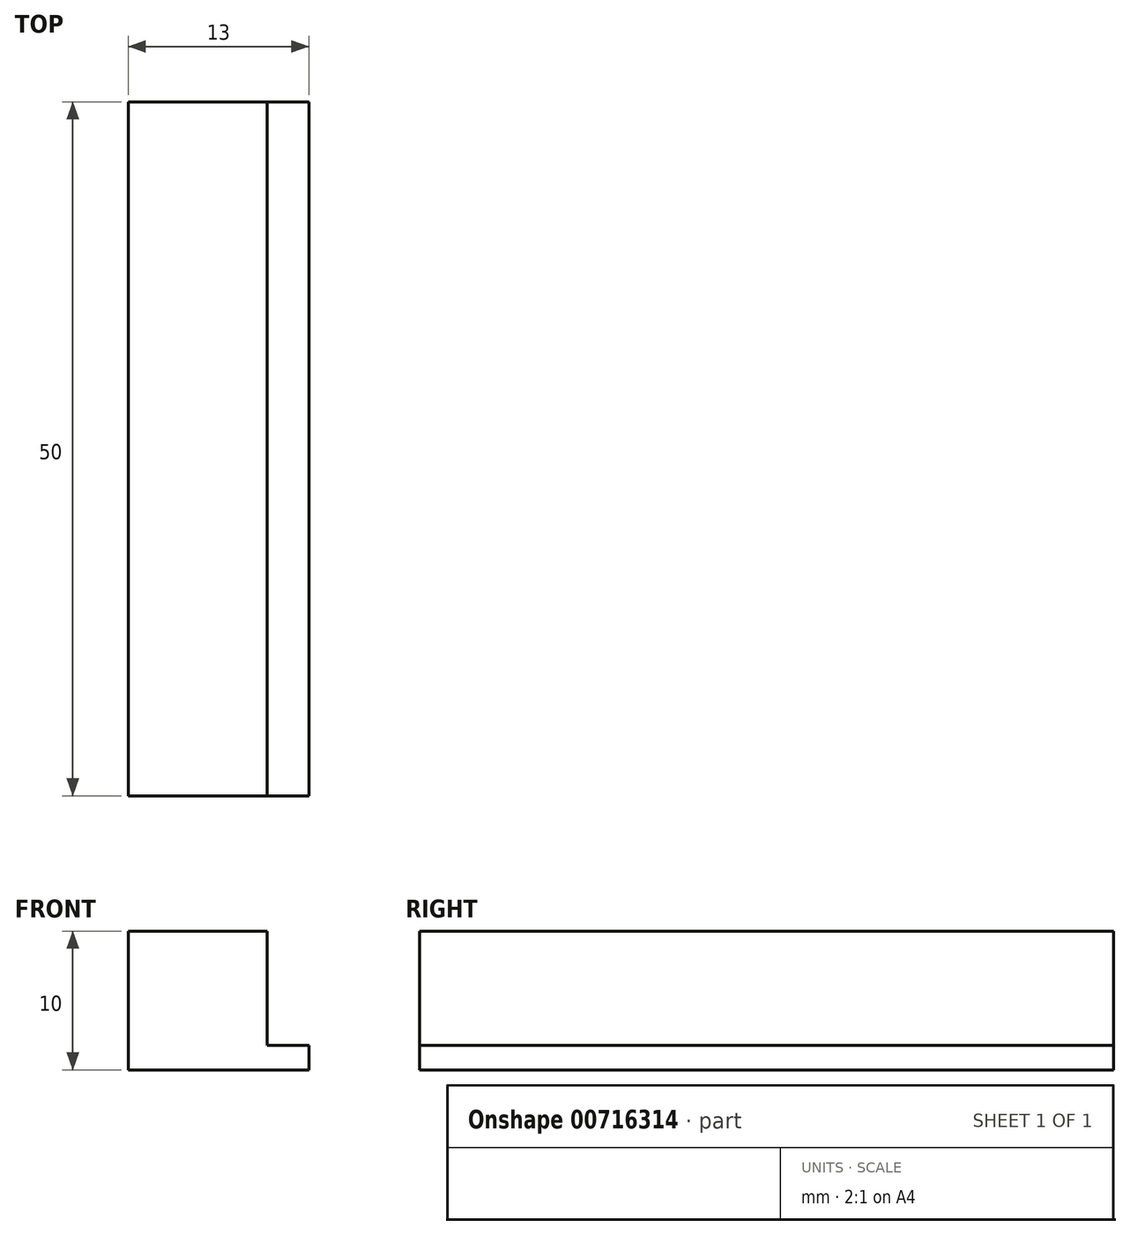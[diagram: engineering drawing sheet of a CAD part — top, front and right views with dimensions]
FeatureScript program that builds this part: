
annotation { "Feature Type Name" : "Feature", "Feature Type Description" : "" }
export const myFeature = defineFeature(function(context is Context, id is Id, definition is map)
    precondition{}
    {
        {
            var Q0;
            Q0=qCreatedBy(makeId("Top.planeOp"),FACE);
            var sketch = newSketch(context, id + "F0", { "sketchPlane" : qUnion([Q0])});
            skLineSegment(sketch, "E0.bottom", {"start": v(0, 0) * mm, "end": v(10, 0) * mm});
            skLineSegment(sketch, "E0.top", {"start": v(0, -50) * mm, "end": v(10, -50) * mm});
            skLineSegment(sketch, "E0.left", {"start": v(0, 0) * mm, "end": v(0, -50) * mm});
            skLineSegment(sketch, "E0.right", {"start": v(10, 0) * mm, "end": v(10, -50) * mm});
            skSolve(sketch);
        }
        {
            var Q0;
            Q0=makeQuery(id+"F0.imprint","IMPRINT",FACE,{"disambiguationData":[TD([[makeQuery(id+"F0.imprint","IMPRINT",EDGE,{"derivedFrom":sQuery(id+"F0.wireOp",EDGE,"E0.bottom")}),-1.0]])]});
            extrude(context, id + "F1", {"entities" : qUnion([Q0]), "depth" : 10 * mm, "offsetDistance" : 25 * mm});
        }
        {
            var Q0;
            Q0=makeQuery(id+"F1.opExtrude","SWEPT_FACE",FACE,{"disambiguationData":[OSD([sQuery(id+"F0.wireOp",EDGE,"E0.right")])]});
            var sketch = newSketch(context, id + "F2", { "sketchPlane" : qUnion([Q0])});
            skLineSegment(sketch, "E1.bottom", {"start": v(-50, 0) * mm, "end": v(0, 0) * mm});
            skLineSegment(sketch, "E1.top", {"start": v(-50, 1.78) * mm, "end": v(0, 1.78) * mm});
            skLineSegment(sketch, "E1.left", {"start": v(-50, 0) * mm, "end": v(-50, 1.78) * mm});
            skLineSegment(sketch, "E1.right", {"start": v(0, 0) * mm, "end": v(0, 1.78) * mm});
            skSolve(sketch);
        }
        {
            var Q0;
            Q0=makeQuery(id+"F2.imprint","IMPRINT",FACE,{"disambiguationData":[TD([[makeQuery(id+"F2.imprint","IMPRINT",EDGE,{"derivedFrom":sQuery(id+"F2.wireOp",EDGE,"E1.bottom")}),-1.0]])]});
            extrude(context, id + "F3", {"entities" : qUnion([Q0]), "operationType" : NewBodyOperationType.ADD, "depth" : 3 * mm, "offsetDistance" : 25 * mm});
        }
    });
